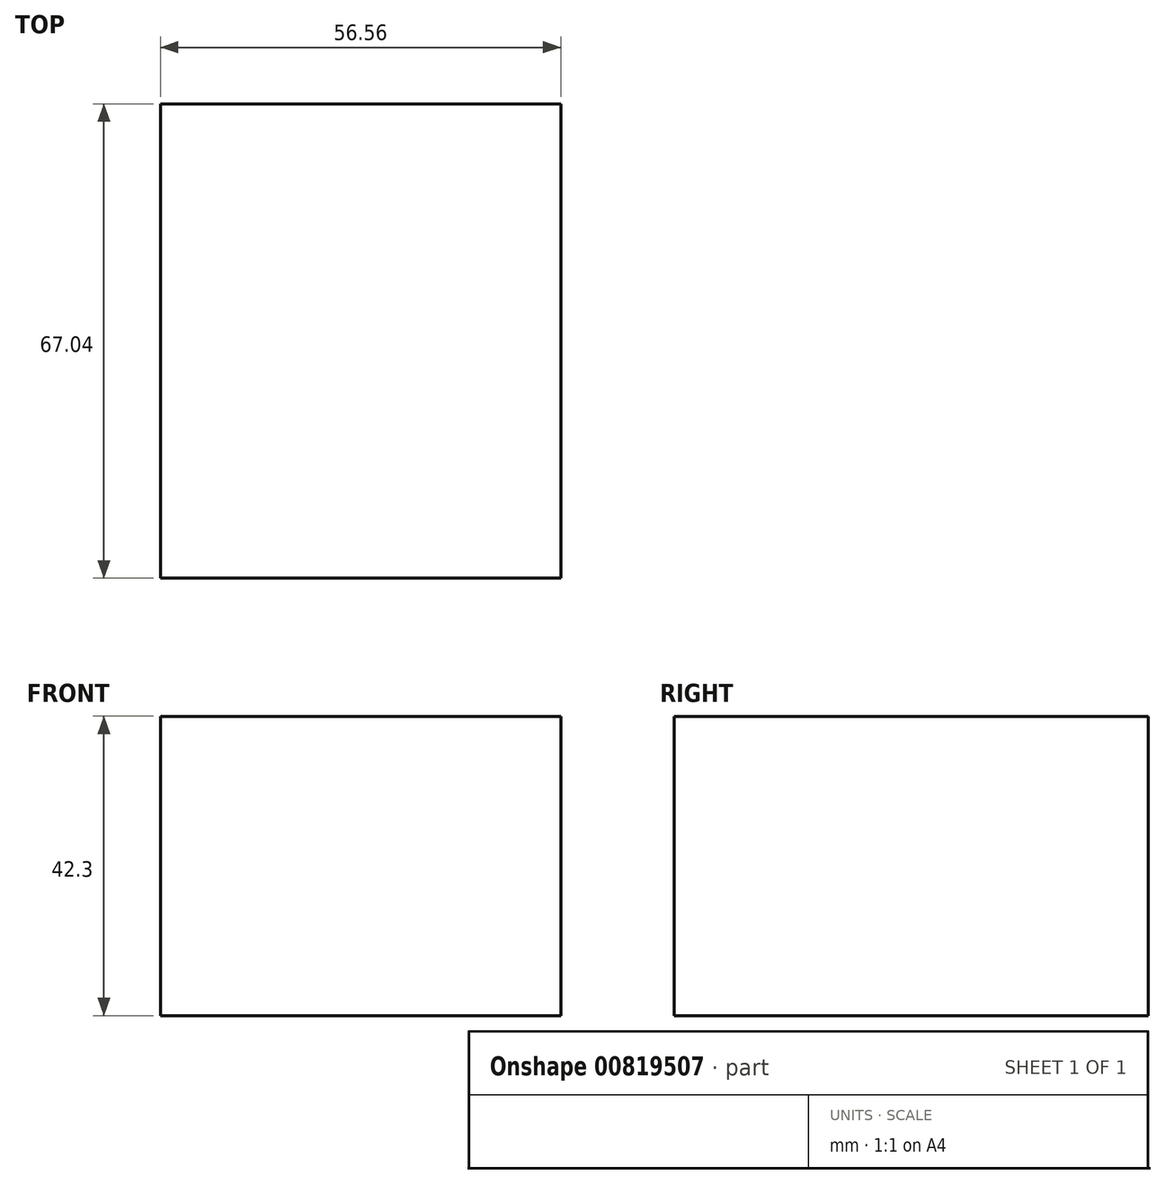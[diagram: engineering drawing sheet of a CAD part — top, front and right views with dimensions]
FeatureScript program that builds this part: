
annotation { "Feature Type Name" : "Feature", "Feature Type Description" : "" }
export const myFeature = defineFeature(function(context is Context, id is Id, definition is map)
    precondition{}
    {
        {
            var Q0;
            Q0=qCreatedBy(makeId("Front.planeOp"),FACE);
            var sketch = newSketch(context, id + "F0", { "sketchPlane" : qUnion([Q0])});
            skLineSegment(sketch, "E0.bottom", {"start": v(56.56, 56.63) * mm, "end": v(0, 56.63) * mm});
            skLineSegment(sketch, "E0.top", {"start": v(56.56, 14.33) * mm, "end": v(0, 14.33) * mm});
            skLineSegment(sketch, "E0.left", {"start": v(56.56, 56.63) * mm, "end": v(56.56, 14.33) * mm});
            skLineSegment(sketch, "E0.right", {"start": v(0, 56.63) * mm, "end": v(0, 14.33) * mm});
            skSolve(sketch);
        }
        {
            var Q0;
            Q0=makeQuery(id+"F0.imprint","IMPRINT",FACE,{"disambiguationData":[TD([[makeQuery(id+"F0.imprint","IMPRINT",EDGE,{"derivedFrom":sQuery(id+"F0.wireOp",EDGE,"E0.bottom")}),1.0]])]});
            extrude(context, id + "F1", {"entities" : qUnion([Q0]), "depth" : 67.04 * mm, "offsetDistance" : 25.4 * mm});
        }
    });
